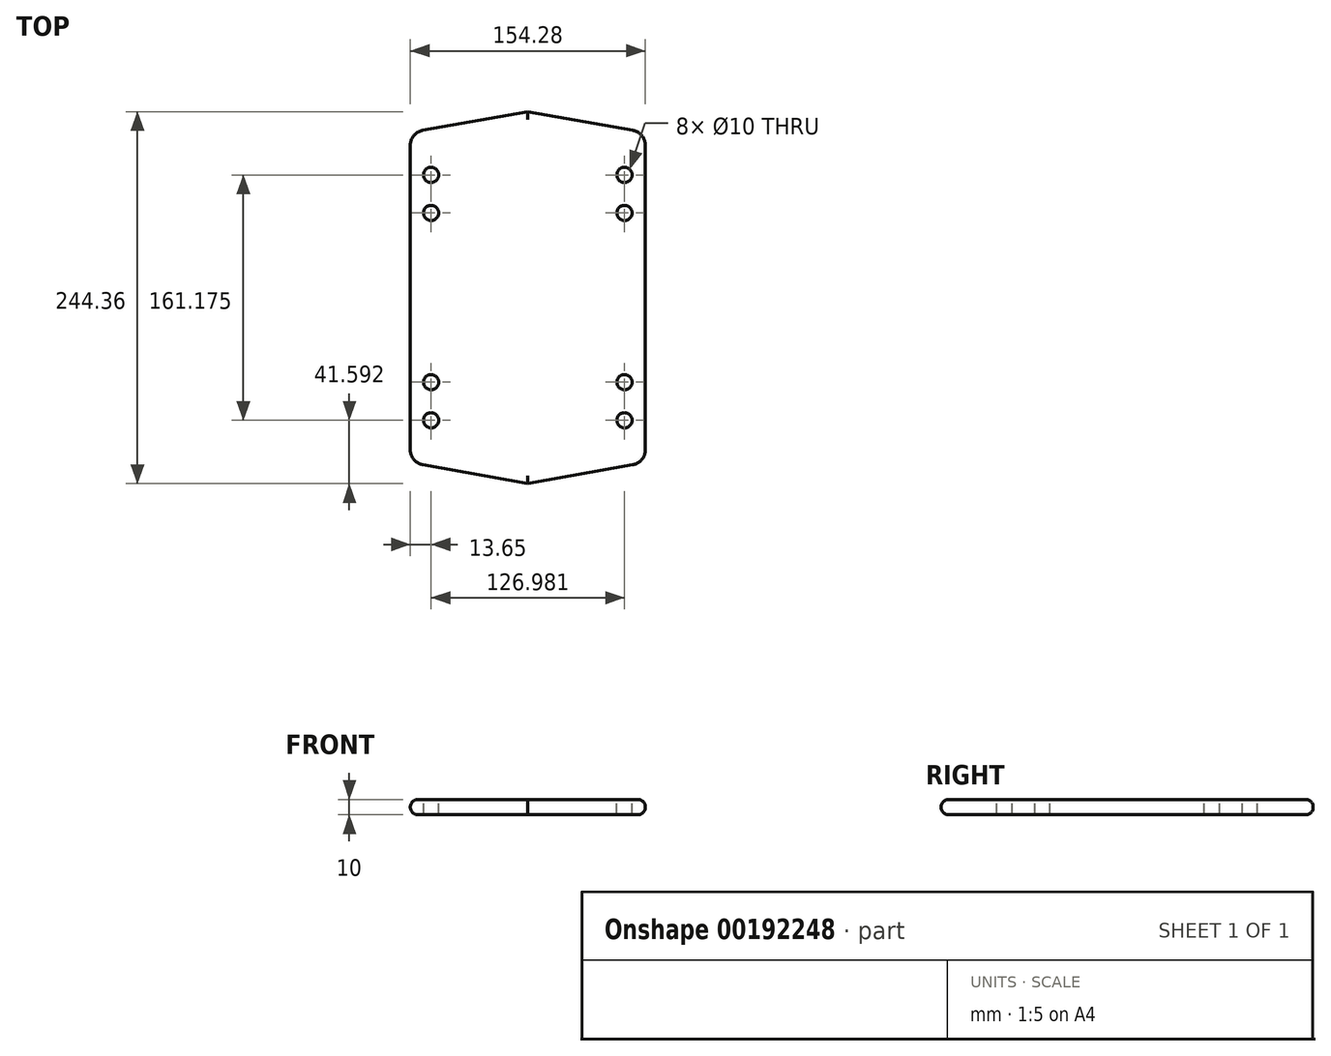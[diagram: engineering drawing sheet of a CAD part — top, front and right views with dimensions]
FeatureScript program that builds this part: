
annotation { "Feature Type Name" : "Feature", "Feature Type Description" : "" }
export const myFeature = defineFeature(function(context is Context, id is Id, definition is map)
    precondition{}
    {
        {
            var Q0;
            Q0=qCreatedBy(makeId("Top.planeOp"),FACE);
            var sketch = newSketch(context, id + "F0", { "sketchPlane" : qUnion([Q0])});
            skLineSegment(sketch, "E0", {"start": v(-68.9, 109.84) * mm, "end": v(0, 122.18) * mm});
            skPoint(sketch, "E1.visualSharp", {"position": v(-77.14, 108.37) * mm});
            skArc(sketch, "E1.filletArc", {"start": v(-68.9, 109.84) * mm, "mid": v(-74.8, 106.42) * mm, "end": v(-77.14, 100) * mm});
            skLineSegment(sketch, "E2.MirrorCS", {"start": v(68.9, 109.84) * mm, "end": v(0, 122.18) * mm});
            skArc(sketch, "E3.MirrorCS", {"start": v(68.9, 109.84) * mm, "mid": v(74.8, 106.42) * mm, "end": v(77.14, 100) * mm});
            skArc(sketch, "E4.MirrorCS", {"start": v(-68.9, -109.84) * mm, "mid": v(-74.8, -106.42) * mm, "end": v(-77.14, -100) * mm});
            skPoint(sketch, "E5.MirrorP", {"position": v(-77.14, -108.37) * mm});
            skLineSegment(sketch, "E6.MirrorCS", {"start": v(-68.9, -109.84) * mm, "end": v(0, -122.18) * mm});
            skLineSegment(sketch, "E7.MirrorCS", {"start": v(68.9, -109.84) * mm, "end": v(0, -122.18) * mm});
            skArc(sketch, "E8.MirrorCS", {"start": v(68.9, -109.84) * mm, "mid": v(74.8, -106.42) * mm, "end": v(77.14, -100) * mm});
            skLineSegment(sketch, "E9", {"start": v(77.14, -100) * mm, "end": v(77.14, 0) * mm});
            skLineSegment(sketch, "E10.MirrorCS", {"start": v(77.14, 100) * mm, "end": v(77.14, 0) * mm});
            skLineSegment(sketch, "E11.MirrorCS", {"start": v(-77.14, -100) * mm, "end": v(-77.14, 0) * mm});
            skLineSegment(sketch, "E12.MirrorCS", {"start": v(-77.14, 100) * mm, "end": v(-77.14, 0) * mm});
            skSolve(sketch);
        }
        {
            var Q0;
            Q0=makeQuery(id+"F0.imprint","IMPRINT",FACE,{"disambiguationData":[TD([[makeQuery(id+"F0.imprint","IMPRINT",EDGE,{"derivedFrom":sQuery(id+"F0.wireOp",EDGE,"E0")}),-1.0]])]});
            extrude(context, id + "F1", {"entities" : qUnion([Q0]), "depth" : 10 * mm});
        }
        {
            var Q0;
            Q0=makeQuery(id+"F1.opExtrude","CAP_FACE",FACE,{"disambiguationData":[OSD([sQuery(id+"F0.wireOp",EDGE,"E0"),sQuery(id+"F0.wireOp",EDGE,"E1.filletArc"),sQuery(id+"F0.wireOp",EDGE,"E2.MirrorCS"),sQuery(id+"F0.wireOp",EDGE,"E3.MirrorCS"),sQuery(id+"F0.wireOp",EDGE,"E4.MirrorCS"),sQuery(id+"F0.wireOp",EDGE,"E6.MirrorCS"),sQuery(id+"F0.wireOp",EDGE,"E7.MirrorCS"),sQuery(id+"F0.wireOp",EDGE,"E8.MirrorCS"),sQuery(id+"F0.wireOp",EDGE,"E9"),sQuery(id+"F0.wireOp",EDGE,"E10.MirrorCS"),sQuery(id+"F0.wireOp",EDGE,"E11.MirrorCS"),sQuery(id+"F0.wireOp",EDGE,"E12.MirrorCS")])],"isStart":false});
            var sketch = newSketch(context, id + "F2", { "sketchPlane" : qUnion([Q0])});
            skCircle(sketch, "E13", {"center": v(63.5, -80.59) * mm, "radius": 5 * mm});
            skCircle(sketch, "E14", {"center": v(63.5, -55.59) * mm, "radius": 5 * mm});
            skCircle(sketch, "E15.MirrorC", {"center": v(-63.5, -80.59) * mm, "radius": 5 * mm});
            skCircle(sketch, "E16.MirrorC", {"center": v(-63.5, -55.59) * mm, "radius": 5 * mm});
            skCircle(sketch, "E17.MirrorC", {"center": v(63.5, 80.59) * mm, "radius": 5 * mm});
            skCircle(sketch, "E18.MirrorC", {"center": v(63.5, 55.59) * mm, "radius": 5 * mm});
            skCircle(sketch, "E19.MirrorC", {"center": v(-63.5, 55.59) * mm, "radius": 5 * mm});
            skCircle(sketch, "E20.MirrorC", {"center": v(-63.5, 80.59) * mm, "radius": 5 * mm});
            skSolve(sketch);
        }
        {
            var Q0;
            Q0=qSketchRegion(id+"F2",true);
            extrude(context, id + "F3", {"entities" : qUnion([Q0]), "operationType" : NewBodyOperationType.REMOVE, "oppositeDirection" : true, "depth" : 25 * mm});
        }
        {
            var Q0;
            Q0=makeQuery(id+"F1.opExtrude","CAP_EDGE",EDGE,{"disambiguationData":[OSD([sQuery(id+"F0.wireOp",EDGE,"E9"),sQuery(id+"F0.wireOp",EDGE,"E10.MirrorCS")])],"isStart":false});
            var Q1;
            Q1=makeQuery(id+"F1.opExtrude","CAP_EDGE",EDGE,{"disambiguationData":[OSD([sQuery(id+"F0.wireOp",EDGE,"E9"),sQuery(id+"F0.wireOp",EDGE,"E10.MirrorCS")])],"isStart":true});
            var Q2;
            Q2=makeQuery(id+"F1.opExtrude","CAP_EDGE",EDGE,{"disambiguationData":[OSD([sQuery(id+"F0.wireOp",EDGE,"E0")])],"isStart":false});
            var Q3;
            Q3=makeQuery(id+"F1.opExtrude","CAP_EDGE",EDGE,{"disambiguationData":[OSD([sQuery(id+"F0.wireOp",EDGE,"E0")])],"isStart":true});
            fillet(context, id + "F4", {"entities" : qUnion([Q0, Q1, Q2, Q3]), "radius" : 5 * mm, "tangentPropagation" : true, "allowEdgeOverflow" : false});
        }
    });
